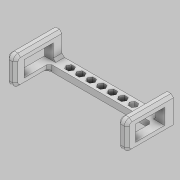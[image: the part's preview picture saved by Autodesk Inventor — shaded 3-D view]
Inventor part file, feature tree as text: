
AUTODESK INVENTOR PART (.ipt)
format: ipt  version: 2022.2 (Build 262287010, 287A)  size: 238,080 bytes
history: native  units: mm
features: extrude x4, sketch x3, chamfer x2, other x1, fillet x1
ambient origin geometry x8: Origin, YZ Plane, XZ Plane, XY Plane, X Axis, Y Axis, Z Axis, Center Point
bodies: Body1 (feature_tree)
feature tree (11):
  other  "Sólido1"
  extrude  "Extrusión1"  Depth=5.5mm
  extrude  "Extrusión2"  Depth=7.0mm TaperAngle=0.0deg
  extrude  "Extrusión7"  Depth=37.0mm
  extrude  "Extrusión8"  Depth=17.5mm TaperAngle=0.0deg
  fillet  "Empalme5"  Radius=12.5mm
  chamfer  "Chaflán3"  Distance=23.0mm
  chamfer  "Chaflán4"  [1 undecoded]
  sketch  "Boceto1"  dims[d14=5.0mm d15=0.0mm d17=5.5mm]
  sketch  "Boceto11"  dims[d20=40.0mm d22=8.4mm d23=10.0mm d25=10.0mm d27=7.0mm d28=0.0mm]
  sketch  "Boceto12"  dims[d70=7.0mm d71=37.0mm d72=17.5mm d73=0.0mm d74=12.5mm d75=23.0mm d76=0.0mm d77=0.0mm d79=4.0mm d80=2.0mm d81=2.0mm d82=45.0deg d83=2.0mm d84=2.0mm d85=45.0deg]
note: 1 required parameter value undecoded (feature->parameter linkage not recoverable at this tier; creation-order binding heuristic only, values carry confidence <= 0.55)
